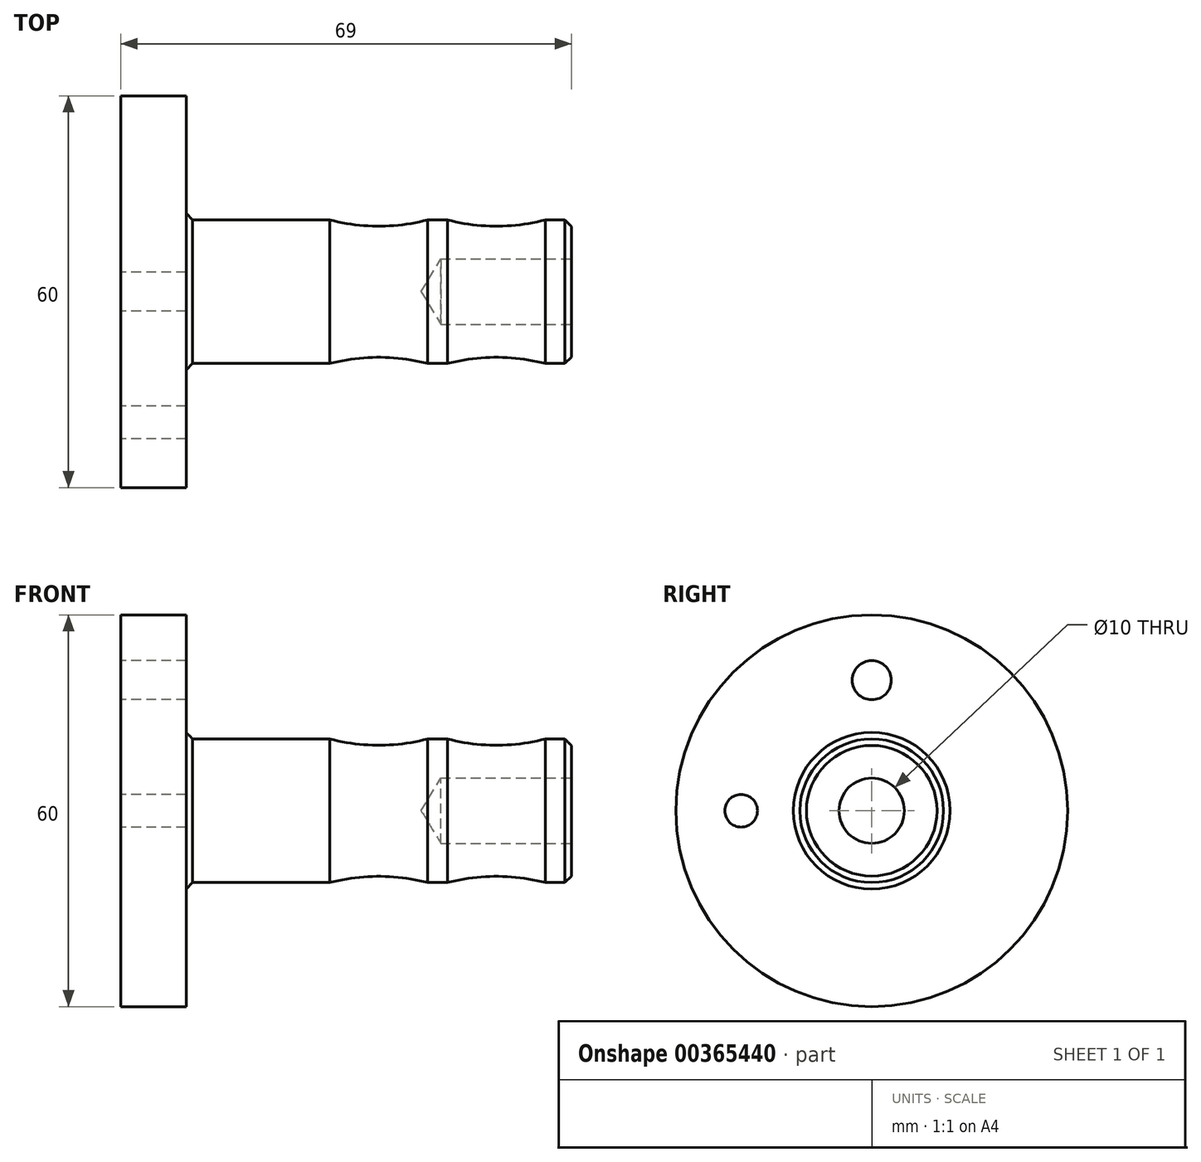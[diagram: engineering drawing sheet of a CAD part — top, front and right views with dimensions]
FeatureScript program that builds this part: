
annotation { "Feature Type Name" : "Feature", "Feature Type Description" : "" }
export const myFeature = defineFeature(function(context is Context, id is Id, definition is map)
    precondition{}
    {
        {
            var Q0;
            Q0=qCreatedBy(makeId("Front.planeOp"),FACE);
            var sketch = newSketch(context, id + "F0", { "sketchPlane" : qUnion([Q0])});
            skLineSegment(sketch, "E0", {"start": v(-59, 12) * mm, "end": v(-59, 30) * mm});
            skLineSegment(sketch, "E1", {"start": v(-59, 30) * mm, "end": v(-69, 30) * mm});
            skLineSegment(sketch, "E2", {"start": v(-69, 30) * mm, "end": v(-69, 0) * mm});
            skLineSegment(sketch, "E3", {"start": v(-69, 0) * mm, "end": v(0, 0) * mm});
            skLineSegment(sketch, "E4", {"start": v(0, 10) * mm, "end": v(-1, 11) * mm});
            skLineSegment(sketch, "E5", {"start": v(-1, 11) * mm, "end": v(-4, 11) * mm});
            skLineSegment(sketch, "E6", {"start": v(0, 10) * mm, "end": v(0, 0) * mm});
            skLineSegment(sketch, "E7.trimOffspring", {"start": v(-19, 11) * mm, "end": v(-22, 11) * mm});
            skArc(sketch, "E8", {"start": v(-19, 11) * mm, "mid": v(-11.5, 10.05) * mm, "end": v(-4, 11) * mm});
            skLineSegment(sketch, "E9", {"start": v(-19, 11) * mm, "end": v(-4, 11) * mm, "construction": true});
            skLineSegment(sketch, "E10", {"start": v(-42.05, 0) * mm, "end": v(4.7, 0) * mm, "construction": true});
            skLineSegment(sketch, "E11", {"start": v(-58, 11) * mm, "end": v(-37, 11) * mm});
            skArc(sketch, "E12", {"start": v(-37, 11) * mm, "mid": v(-29.5, 10.05) * mm, "end": v(-22, 11) * mm});
            skLineSegment(sketch, "E13", {"start": v(-37, 11) * mm, "end": v(-22, 11) * mm, "construction": true});
            skLineSegment(sketch, "E14", {"start": v(-49, 25.37) * mm, "end": v(-49, 3.27) * mm, "construction": true});
            skLineSegment(sketch, "E15", {"start": v(-58, 11) * mm, "end": v(-59, 12) * mm});
            skPoint(sketch, "E16.orphan", {"position": v(-59, 11) * mm});
            skSolve(sketch);
        }
        {
            var Q0;
            Q0 = qSketchRegion(id + "F0", true);
            var Q1;
            Q1=sQuery(id+"F0.wireOp",EDGE,"E10");
            revolve(context, id + "F1", {"entities" : qUnion([Q0]), "axis" : qUnion([Q1]), "revolveType" : RevolveType.FULL});
        }
        {
            var Q0;
            Q0=makeQuery(id+"F1.opRevolve","SWEPT_FACE",FACE,{"disambiguationData":[OSD([sQuery(id+"F0.wireOp",EDGE,"E2")])]});
            var sketch = newSketch(context, id + "F2", { "sketchPlane" : qUnion([Q0])});
            skPoint(sketch, "E17", {"position": v(0, 20) * mm});
            skSolve(sketch);
        }
        {
            var Q0;
            Q0=sQuery(id+"F2.wireOp",VERTEX,"E17");
            var Q1;
            Q1=makeQuery(id+"F1.opRevolve","SWEPT_BODY",BODY,{"disambiguationData":[OSD([sQuery(id+"F0.wireOp",EDGE,"E0"),sQuery(id+"F0.wireOp",EDGE,"E1"),sQuery(id+"F0.wireOp",EDGE,"E2"),sQuery(id+"F0.wireOp",EDGE,"E3"),sQuery(id+"F0.wireOp",EDGE,"E4"),sQuery(id+"F0.wireOp",EDGE,"E5"),sQuery(id+"F0.wireOp",EDGE,"E6"),sQuery(id+"F0.wireOp",EDGE,"E7.trimOffspring"),sQuery(id+"F0.wireOp",EDGE,"E8"),sQuery(id+"F0.wireOp",EDGE,"E11"),sQuery(id+"F0.wireOp",EDGE,"E12")])]});
            hole(context, id + "F3", {"style" : HoleStyle.SIMPLE, "endStyle" : HoleEndStyle.THROUGH, "holeDiameter" : 6 * mm, "isTappedThrough" : true, "tappedDepth" : 12 * mm, "tapClearance" : 3, "locations" : qUnion([Q0]), "scope" : qUnion([Q1])});
        }
        {
            var Q0;
            Q0=makeQuery(id+"F1.opRevolve","SWEPT_FACE",FACE,{"disambiguationData":[OSD([sQuery(id+"F0.wireOp",EDGE,"E2")])]});
            var sketch = newSketch(context, id + "F4", { "sketchPlane" : qUnion([Q0])});
            skPoint(sketch, "E18", {"position": v(20, 0) * mm});
            skSolve(sketch);
        }
        {
            var Q0;
            Q0=sQuery(id+"F4.wireOp",VERTEX,"E18");
            var Q1;
            Q1=makeQuery(id+"F1.opRevolve","SWEPT_BODY",BODY,{"disambiguationData":[OSD([sQuery(id+"F0.wireOp",EDGE,"E0"),sQuery(id+"F0.wireOp",EDGE,"E1"),sQuery(id+"F0.wireOp",EDGE,"E2"),sQuery(id+"F0.wireOp",EDGE,"E3"),sQuery(id+"F0.wireOp",EDGE,"E4"),sQuery(id+"F0.wireOp",EDGE,"E5"),sQuery(id+"F0.wireOp",EDGE,"E6"),sQuery(id+"F0.wireOp",EDGE,"E7.trimOffspring"),sQuery(id+"F0.wireOp",EDGE,"E8"),sQuery(id+"F0.wireOp",EDGE,"E11"),sQuery(id+"F0.wireOp",EDGE,"E12")])]});
            hole(context, id + "F5", {"style" : HoleStyle.SIMPLE, "endStyle" : HoleEndStyle.THROUGH, "holeDiameter" : 5 * mm, "isTappedThrough" : true, "tappedDepth" : 12 * mm, "tapClearance" : 3, "locations" : qUnion([Q0]), "scope" : qUnion([Q1])});
        }
        {
            var Q0;
            Q0=makeQuery(id+"F1.opRevolve","SWEPT_FACE",FACE,{"disambiguationData":[OSD([sQuery(id+"F0.wireOp",EDGE,"E6")])]});
            var sketch = newSketch(context, id + "F6", { "sketchPlane" : qUnion([Q0])});
            skPoint(sketch, "E19", {"position": v(0, 0) * mm});
            skSolve(sketch);
        }
        {
            var Q0;
            Q0=sQuery(id+"F6.wireOp",VERTEX,"E19");
            var Q1;
            Q1=makeQuery(id+"F1.opRevolve","SWEPT_BODY",BODY,{"disambiguationData":[OSD([sQuery(id+"F0.wireOp",EDGE,"E0"),sQuery(id+"F0.wireOp",EDGE,"E1"),sQuery(id+"F0.wireOp",EDGE,"E2"),sQuery(id+"F0.wireOp",EDGE,"E3"),sQuery(id+"F0.wireOp",EDGE,"E4"),sQuery(id+"F0.wireOp",EDGE,"E5"),sQuery(id+"F0.wireOp",EDGE,"E6"),sQuery(id+"F0.wireOp",EDGE,"E7.trimOffspring"),sQuery(id+"F0.wireOp",EDGE,"E8"),sQuery(id+"F0.wireOp",EDGE,"E11"),sQuery(id+"F0.wireOp",EDGE,"E12")])]});
            hole(context, id + "F7", {"style" : HoleStyle.SIMPLE, "endStyle" : HoleEndStyle.BLIND, "holeDiameter" : 10 * mm, "holeDepth" : 20 * mm, "isTappedThrough" : true, "tappedDepth" : 12 * mm, "tapClearance" : 3, "locations" : qUnion([Q0]), "scope" : qUnion([Q1])});
        }
    });
